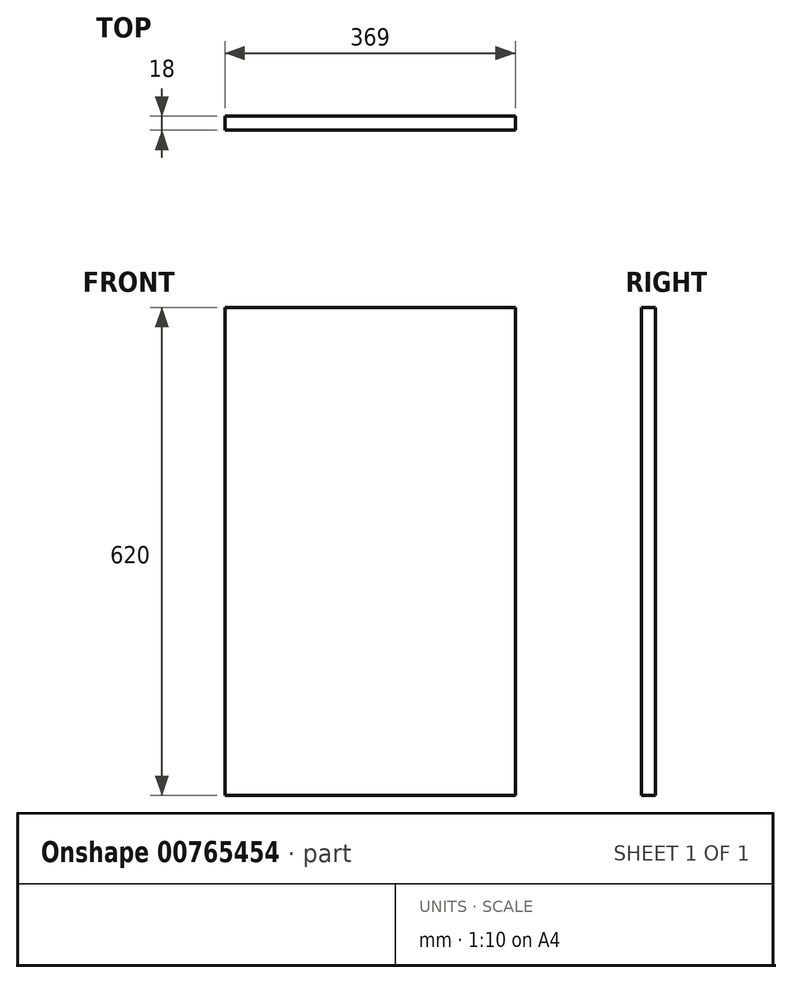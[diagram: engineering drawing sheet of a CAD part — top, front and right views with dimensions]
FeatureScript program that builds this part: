
annotation { "Feature Type Name" : "Feature", "Feature Type Description" : "" }
export const myFeature = defineFeature(function(context is Context, id is Id, definition is map)
    precondition{}
    {
        {
            var Q0;
            Q0=qCreatedBy(makeId("Front.planeOp"),FACE);
            var sketch = newSketch(context, id + "F0", { "sketchPlane" : qUnion([Q0])});
            skLineSegment(sketch, "E0.bottom", {"start": v(-184.5, -310) * mm, "end": v(184.5, -310) * mm});
            skLineSegment(sketch, "E0.top", {"start": v(-184.5, 310) * mm, "end": v(184.5, 310) * mm});
            skLineSegment(sketch, "E0.left", {"start": v(-184.5, -310) * mm, "end": v(-184.5, 310) * mm});
            skLineSegment(sketch, "E0.right", {"start": v(184.5, -310) * mm, "end": v(184.5, 310) * mm});
            skPoint(sketch, "E0.middle", {"position": v(0, 0) * mm});
            skSolve(sketch);
        }
        {
            var Q0;
            Q0 = qSketchRegion(id + "F0", true);
            extrude(context, id + "F1", {"entities" : qUnion([Q0]), "depth" : 18 * mm, "offsetDistance" : 25 * mm});
        }
    });
